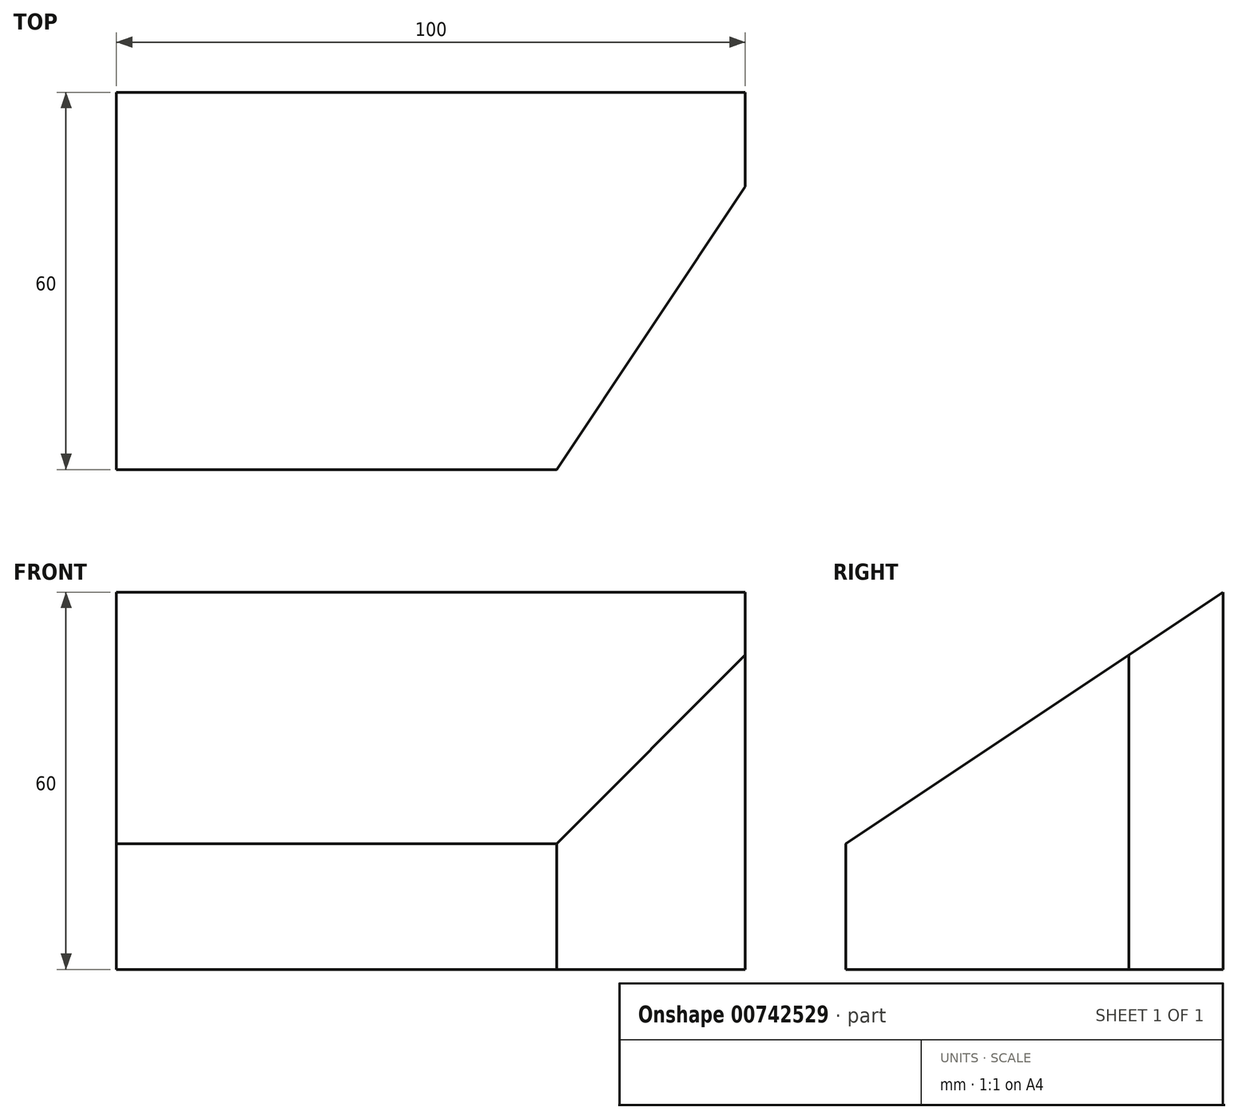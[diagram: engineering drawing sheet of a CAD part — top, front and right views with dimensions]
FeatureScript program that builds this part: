
annotation { "Feature Type Name" : "Feature", "Feature Type Description" : "" }
export const myFeature = defineFeature(function(context is Context, id is Id, definition is map)
    precondition{}
    {
        {
            var Q0;
            Q0=qCreatedBy(makeId("Top.planeOp"),FACE);
            var sketch = newSketch(context, id + "F0", { "sketchPlane" : qUnion([Q0])});
            skLineSegment(sketch, "E0", {"start": v(0, 0) * mm, "end": v(70, 0) * mm});
            skLineSegment(sketch, "E1", {"start": v(0, 60) * mm, "end": v(0, 0) * mm});
            skLineSegment(sketch, "E2", {"start": v(70, 0) * mm, "end": v(100, 45) * mm});
            skLineSegment(sketch, "E3", {"start": v(100, 45) * mm, "end": v(100, 60) * mm});
            skLineSegment(sketch, "E4", {"start": v(0, 60) * mm, "end": v(100, 60) * mm});
            skSolve(sketch);
        }
        {
            var Q0;
            Q0 = qSketchRegion(id + "F0", true);
            extrude(context, id + "F1", {"entities" : qUnion([Q0]), "depth" : 60 * mm, "offsetDistance" : 25 * mm});
        }
        {
            var Q0;
            Q0=makeQuery(id+"F1.opExtrude","SWEPT_FACE",FACE,{"disambiguationData":[OSD([sQuery(id+"F0.wireOp",EDGE,"E1")])]});
            var sketch = newSketch(context, id + "F2", { "sketchPlane" : qUnion([Q0])});
            skLineSegment(sketch, "E5", {"start": v(-60, 60) * mm, "end": v(0, 20) * mm});
            skSolve(sketch);
        }
        {
            var Q0;
            {var subQ0=sQuery(id+"F2.wireOp",EDGE,"E5");Q0=makeQuery(id+"F2.imprint","IMPRINT",FACE,{"disambiguationData":[TD([[makeQuery(id+"F2.imprint","IMPRINT",EDGE,{"derivedFrom":subQ0}),1.0]])]});}
            extrude(context, id + "F3", {"entities" : qUnion([Q0]), "operationType" : NewBodyOperationType.REMOVE, "endBound" : BoundingType.THROUGH_ALL, "oppositeDirection" : true, "depth" : 25 * mm, "offsetDistance" : 25 * mm});
        }
    });
